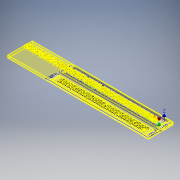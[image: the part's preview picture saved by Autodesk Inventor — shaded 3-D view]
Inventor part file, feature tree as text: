
AUTODESK INVENTOR PART (.ipt)
format: ipt  version: 2018.3 (Build 223284000, 284)  size: 20,308,992 bytes
history: native  units: in
note: dims shown in document units (in); Inventor stores cm internally (conversion verified against a paired STEP export)
features: other x459, extrude x4, plane x2, pattern_linear x2, hole x1
ambient origin geometry x8: Origin, YZ Plane, XZ Plane, XY Plane, X Axis, Y Axis, Z Axis, Center Point
bodies: Solid1 (feature_tree), Solid10 (feature_tree), Solid11 (feature_tree), Solid12 (feature_tree), Solid13 (feature_tree), Solid22 (feature_tree), Solid23 (feature_tree), Solid24 (feature_tree), Solid29 (feature_tree), Solid30 (feature_tree), Solid31 (feature_tree), Solid32 (feature_tree), Solid33 (feature_tree), Solid34 (feature_tree), Solid35 (feature_tree), Solid36 (feature_tree), Solid37 (feature_tree), Solid38 (feature_tree), Solid49 (feature_tree), Solid50 (feature_tree), Solid59 (feature_tree), Solid60 (feature_tree), Solid71 (feature_tree), Solid72 (feature_tree), Solid85 (feature_tree), Solid86 (feature_tree), Solid87 (feature_tree), Solid88 (feature_tree), Solid89 (feature_tree), Solid90 (feature_tree), Solid91 (feature_tree), Solid92 (feature_tree), Solid93 (feature_tree), Solid94 (feature_tree), Solid95 (feature_tree), Solid96 (feature_tree), Solid97 (feature_tree), Solid98 (feature_tree), Solid99 (feature_tree), Solid100 (feature_tree), Solid101 (feature_tree), Solid102 (feature_tree), Solid103 (feature_tree), Solid104 (feature_tree), Solid105 (feature_tree), Solid106 (feature_tree), Solid107 (feature_tree), Solid108 (feature_tree), Solid109 (feature_tree), Solid110 (feature_tree), Solid111 (feature_tree), Solid112 (feature_tree), Solid113 (feature_tree), Solid114 (feature_tree), Solid115 (feature_tree), Solid116 (feature_tree), Solid117 (feature_tree), Solid118 (feature_tree), Solid119 (feature_tree), Solid120 (feature_tree), Solid121 (feature_tree), Solid122 (feature_tree), Solid123 (feature_tree), Solid124 (feature_tree), Solid125 (feature_tree), Solid126 (feature_tree), Solid127 (feature_tree), Solid128 (feature_tree), Solid129 (feature_tree), Solid130 (feature_tree), Solid131 (feature_tree), Solid132 (feature_tree), Solid133 (feature_tree), Solid134 (feature_tree), Solid135 (feature_tree), Solid136 (feature_tree), Solid137 (feature_tree), Solid138 (feature_tree), Solid139 (feature_tree), Solid140 (feature_tree), Solid141 (feature_tree), Solid142 (feature_tree), Solid143 (feature_tree), Solid144 (feature_tree), Solid145 (feature_tree), Solid146 (feature_tree), Solid147 (feature_tree), Solid148 (feature_tree), Solid149 (feature_tree), Solid150 (feature_tree), Solid151 (feature_tree), Solid152 (feature_tree), Solid153 (feature_tree), Solid154 (feature_tree), Solid155 (feature_tree), Solid156 (feature_tree), Solid157 (feature_tree), Solid158 (feature_tree), Solid159 (feature_tree), Solid160 (feature_tree), Solid161 (feature_tree), Solid162 (feature_tree), Solid163 (feature_tree), Solid164 (feature_tree), Solid165 (feature_tree), Solid166 (feature_tree), Solid167 (feature_tree), Solid168 (feature_tree), Solid169 (feature_tree), Solid170 (feature_tree), Solid171 (feature_tree), Solid172 (feature_tree), Solid173 (feature_tree), Solid174 (feature_tree), Solid175 (feature_tree), Solid176 (feature_tree), Solid177 (feature_tree), Solid178 (feature_tree), Solid179 (feature_tree), Solid180 (feature_tree), Solid181 (feature_tree), Solid182 (feature_tree), Solid183 (feature_tree), Solid184 (feature_tree), Solid185 (feature_tree), Solid186 (feature_tree), Solid187 (feature_tree), Solid188 (feature_tree), Solid189 (feature_tree), Solid190 (feature_tree), Solid191 (feature_tree), Solid192 (feature_tree), Solid193 (feature_tree), Solid194 (feature_tree), Solid195 (feature_tree), Solid196 (feature_tree), Solid197 (feature_tree), Solid198 (feature_tree), Solid199 (feature_tree), Solid200 (feature_tree), Solid201 (feature_tree), Solid202 (feature_tree), Solid203 (feature_tree), Solid204 (feature_tree), Solid205 (feature_tree), Solid206 (feature_tree), Solid207 (feature_tree), Solid208 (feature_tree), Solid209 (feature_tree), Solid210 (feature_tree)
feature tree (468):
  other  "Button Fixture Assembly.iam"
  other  "Button Fixture Base.ipt:1"
  other  "Case Buttons CAM.ipt:9"
  other  "Case Buttons CAM.ipt:10"
  other  "Case Buttons CAM.ipt:11"
  other  "Case Buttons CAM.ipt:12"
  other  "Case Buttons CAM.ipt:17"
  other  "Case Buttons CAM.ipt:18"
  other  "Case Buttons CAM.ipt:19"
  other  "Case Buttons CAM.ipt:20"
  other  "Case Buttons CAM.ipt:25"
  other  "Case Buttons CAM.ipt:26"
  other  "Case Buttons CAM.ipt:27"
  other  "Case Buttons CAM.ipt:28"
  other  "Case Buttons CAM.ipt:29"
  other  "Case Buttons CAM.ipt:30"
  other  "Case Buttons CAM.ipt:31"
  other  "Case Buttons CAM.ipt:32"
  other  "Case Buttons CAM.ipt:41"
  other  "Case Buttons CAM.ipt:42"
  other  "Case Buttons CAM.ipt:53"
  other  "Case Buttons CAM.ipt:54"
  other  "Case Buttons CAM.ipt:64"
  other  "Case Buttons CAM.ipt:65"
  other  "Case Buttons CAM.ipt:76"
  other  "Case Buttons CAM.ipt:77"
  other  "Case Buttons CAM.ipt:90"
  other  "Case Buttons CAM.ipt:91"
  other  "Case Buttons CAM.ipt:92"
  other  "Case Buttons CAM.ipt:93"
  other  "Case Buttons CAM.ipt:94"
  other  "Case Buttons CAM.ipt:95"
  other  "Case Buttons CAM.ipt:108"
  other  "Case Buttons CAM.ipt:109"
  other  "Case Buttons CAM.ipt:110"
  other  "Case Buttons CAM.ipt:111"
  other  "Case Buttons CAM.ipt:112"
  other  "Case Buttons CAM.ipt:113"
  other  "Case Buttons CAM.ipt:126"
  other  "Case Buttons CAM.ipt:127"
  other  "Case Buttons CAM.ipt:128"
  other  "Case Buttons CAM.ipt:129"
  other  "Case Buttons CAM.ipt:130"
  other  "Case Buttons CAM.ipt:131"
  other  "Case Buttons CAM.ipt:132"
  other  "Case Buttons CAM.ipt:133"
  other  "Case Buttons CAM.ipt:134"
  other  "Case Buttons CAM.ipt:135"
  other  "Case Buttons CAM.ipt:136"
  other  "Case Buttons CAM.ipt:137"
  other  "Case Buttons CAM.ipt:138"
  other  "Case Buttons CAM.ipt:139"
  other  "Case Buttons CAM.ipt:140"
  other  "Case Buttons CAM.ipt:141"
  other  "Case Buttons CAM.ipt:142"
  other  "Case Buttons CAM.ipt:143"
  other  "Case Buttons CAM.ipt:144"
  other  "Case Buttons CAM.ipt:145"
  other  "Case Buttons CAM.ipt:146"
  other  "Case Buttons CAM.ipt:147"
  other  "Case Buttons CAM.ipt:148"
  other  "Case Buttons CAM.ipt:149"
  other  "Case Buttons CAM.ipt:150"
  other  "Case Buttons CAM.ipt:151"
  other  "Case Buttons CAM.ipt:152"
  other  "Case Buttons CAM.ipt:153"
  other  "Case Buttons CAM.ipt:154"
  other  "Case Buttons CAM.ipt:155"
  other  "Case Buttons CAM.ipt:156"
  other  "Case Buttons CAM.ipt:157"
  other  "Case Buttons CAM.ipt:158"
  other  "Case Buttons CAM.ipt:159"
  other  "Case Buttons CAM.ipt:160"
  other  "Case Buttons CAM.ipt:161"
  other  "Case Buttons CAM.ipt:162"
  other  "Case Buttons CAM.ipt:163"
  other  "Case Buttons CAM.ipt:164"
  other  "Case Buttons CAM.ipt:165"
  other  "Case Buttons CAM.ipt:166"
  other  "Case Buttons CAM.ipt:167"
  other  "Case Buttons CAM.ipt:168"
  other  "Case Buttons CAM.ipt:169"
  other  "Case Buttons CAM.ipt:170"
  other  "Case Buttons CAM.ipt:171"
  other  "Case Buttons CAM.ipt:172"
  other  "Case Buttons CAM.ipt:173"
  other  "Case Buttons CAM.ipt:174"
  other  "Case Buttons CAM.ipt:175"
  other  "Case Buttons CAM.ipt:176"
  other  "Case Buttons CAM.ipt:177"
  other  "Case Buttons CAM.ipt:178"
  other  "Case Buttons CAM.ipt:179"
  other  "Case Buttons CAM.ipt:180"
  other  "Case Buttons CAM.ipt:181"
  other  "Case Buttons CAM.ipt:182"
  other  "Case Buttons CAM.ipt:183"
  other  "Case Buttons CAM.ipt:184"
  other  "Case Buttons CAM.ipt:185"
  other  "Case Buttons CAM.ipt:186"
  other  "Case Buttons CAM.ipt:187"
  other  "Case Buttons CAM.ipt:188"
  other  "Case Buttons CAM.ipt:189"
  other  "Case Buttons CAM.ipt:190"
  other  "Case Buttons CAM.ipt:191"
  other  "Case Buttons CAM.ipt:192"
  other  "Case Buttons CAM.ipt:193"
  other  "Case Buttons CAM.ipt:194"
  other  "Case Buttons CAM.ipt:195"
  other  "Case Buttons CAM.ipt:196"
  other  "Case Buttons CAM.ipt:197"
  other  "Case Buttons CAM.ipt:198"
  other  "Case Buttons CAM.ipt:199"
  other  "Case Buttons CAM.ipt:200"
  other  "Case Buttons CAM.ipt:201"
  other  "Case Buttons CAM.ipt:202"
  other  "Case Buttons CAM.ipt:203"
  other  "Case Buttons CAM.ipt:204"
  other  "Case Buttons CAM.ipt:205"
  other  "Case Buttons CAM.ipt:206"
  other  "Case Buttons CAM.ipt:207"
  other  "Case Buttons CAM.ipt:208"
  other  "Case Buttons CAM.ipt:209"
  other  "Case Buttons CAM.ipt:210"
  other  "Case Buttons CAM.ipt:211"
  other  "Case Buttons CAM.ipt:212"
  other  "Case Buttons CAM.ipt:213"
  other  "Case Buttons CAM.ipt:214"
  other  "Case Buttons CAM.ipt:215"
  other  "Case Buttons CAM.ipt:216"
  other  "Case Buttons CAM.ipt:217"
  other  "Case Buttons CAM.ipt:218"
  other  "Case Buttons CAM.ipt:219"
  other  "Case Buttons CAM.ipt:220"
  other  "Case Buttons CAM.ipt:221"
  other  "Case Buttons CAM.ipt:222"
  other  "Case Buttons CAM.ipt:223"
  other  "Case Buttons CAM.ipt:224"
  other  "Case Buttons CAM.ipt:225"
  other  "Case Buttons CAM.ipt:226"
  other  "Case Buttons CAM.ipt:227"
  other  "Case Buttons CAM.ipt:228"
  other  "Case Buttons CAM.ipt:229"
  other  "Case Buttons CAM.ipt:230"
  other  "Case Buttons CAM.ipt:231"
  other  "Case Buttons CAM.ipt:232"
  other  "Case Buttons CAM.ipt:233"
  other  "Case Buttons CAM.ipt:234"
  other  "Case Buttons CAM.ipt:235"
  other  "Case Buttons CAM.ipt:236"
  other  "Case Buttons CAM.ipt:237"
  other  "Case Buttons CAM.ipt:238"
  other  "Case Buttons CAM.ipt:239"
  plane  "Work Plane1"
  plane  "Work Plane3"
  extrude  "Extrusion20"  Depth=0.3937in
  extrude  "Extrusion19"  Depth=0.3in TaperAngle=0.0deg
  hole  "Hole1"  [1 undecoded]
  pattern_linear  "Rectangular Pattern6"  Spacing1=0.0in  [1 undecoded]
  pattern_linear  "Rectangular Pattern7"  Count1=3 Spacing1=7.75in
  other  "Hold Down Sketch 1"
  other  "Hold Down Sketch 2"
  extrude  "Extrusion22"  Depth=0.0156in TaperAngle=0.0deg
  extrude  "Extrusion23"  Depth=0.0156in TaperAngle=0.0deg
  other  "Origin Sketch"
  other  "Vacuum Sketch"
  other  "Vacuum Sketch_1"
  other  "Vacuum Sketch_2"
  other  "Vacuum Sketch_3"
  other  "Button Peg Sketch"
  other  "Button Peg Sketch_1"
  other  "Button Peg Sketch_2"
  other  "Button Peg Sketch_3"
  other  "First Contour Solid"
  other  "Vacuum Sketch_4"
  other  "Button Peg Sketch_8"
  other  "Vacuum Sketch_5"
  other  "Button Peg Sketch_9"
  other  "Vacuum Sketch_6"
  other  "Button Peg Sketch_10"
  other  "Vacuum Sketch_7"
  other  "Button Peg Sketch_11"
  other  "Vacuum Sketch_8"
  other  "Button Peg Sketch_12"
  other  "Vacuum Sketch_9"
  other  "Button Peg Sketch_13"
  other  "Vacuum Sketch_10"
  other  "Button Peg Sketch_14"
  other  "Vacuum Sketch_11"
  other  "Button Peg Sketch_15"
  other  "Vacuum Sketch_12"
  other  "Button Peg Sketch_16"
  other  "Vacuum Sketch_13"
  other  "Button Peg Sketch_17"
  other  "Vacuum Sketch_14"
  other  "Button Peg Sketch_18"
  other  "Vacuum Sketch_15"
  other  "Button Peg Sketch_19"
  other  "Contour Boundary Sketch"
  other  "Pocket Boundary Sketch"
  other  "Contour Standoff Boundary Sketch"
  other  "Vacuum Sketch_16"
  other  "Button Peg Sketch_20"
  other  "Vacuum Sketch_17"
  other  "Button Peg Sketch_21"
  other  "Vacuum Sketch_28"
  other  "Button Peg Sketch_32"
  other  "Vacuum Sketch_29"
  other  "Button Peg Sketch_33"
  other  "Vacuum Sketch_38"
  other  "Button Peg Sketch_42"
  other  "Vacuum Sketch_39"
  other  "Button Peg Sketch_43"
  other  "Vacuum Sketch_50"
  other  "Button Peg Sketch_54"
  other  "Vacuum Sketch_51"
  other  "Button Peg Sketch_55"
  other  "Vacuum Sketch_52"
  other  "Button Peg Sketch_66"
  other  "Vacuum Sketch_53"
  other  "Button Peg Sketch_67"
  other  "Vacuum Sketch_54"
  other  "Button Peg Sketch_68"
  other  "Vacuum Sketch_55"
  other  "Button Peg Sketch_69"
  other  "Vacuum Sketch_56"
  other  "Button Peg Sketch_70"
  other  "Vacuum Sketch_57"
  other  "Button Peg Sketch_71"
  other  "Vacuum Sketch_58"
  other  "Button Peg Sketch_72"
  other  "Vacuum Sketch_59"
  other  "Button Peg Sketch_73"
  other  "Vacuum Sketch_60"
  other  "Button Peg Sketch_74"
  other  "Vacuum Sketch_61"
  other  "Button Peg Sketch_75"
  other  "Vacuum Sketch_62"
  other  "Button Peg Sketch_76"
  other  "Vacuum Sketch_63"
  other  "Button Peg Sketch_77"
  other  "Vacuum Sketch_64"
  other  "Button Peg Sketch_78"
  other  "Vacuum Sketch_65"
  other  "Button Peg Sketch_79"
  other  "Vacuum Sketch_66"
  other  "Button Peg Sketch_80"
  other  "Vacuum Sketch_67"
  other  "Button Peg Sketch_81"
  other  "Vacuum Sketch_68"
  other  "Button Peg Sketch_82"
  other  "Vacuum Sketch_69"
  other  "Button Peg Sketch_83"
  other  "Vacuum Sketch_70"
  other  "Button Peg Sketch_84"
  other  "Vacuum Sketch_71"
  other  "Button Peg Sketch_85"
  other  "Vacuum Sketch_72"
  other  "Button Peg Sketch_86"
  other  "Vacuum Sketch_73"
  other  "Button Peg Sketch_87"
  other  "Vacuum Sketch_74"
  other  "Button Peg Sketch_88"
  other  "Vacuum Sketch_75"
  other  "Button Peg Sketch_89"
  other  "Vacuum Sketch_76"
  other  "Button Peg Sketch_90"
  other  "Vacuum Sketch_77"
  other  "Button Peg Sketch_91"
  other  "Vacuum Sketch_78"
  other  "Button Peg Sketch_92"
  other  "Vacuum Sketch_79"
  other  "Button Peg Sketch_93"
  other  "Vacuum Sketch_80"
  other  "Button Peg Sketch_94"
  other  "Vacuum Sketch_81"
  other  "Button Peg Sketch_95"
  other  "Vacuum Sketch_82"
  other  "Button Peg Sketch_96"
  other  "Vacuum Sketch_83"
  other  "Button Peg Sketch_97"
  other  "Vacuum Sketch_84"
  other  "Button Peg Sketch_98"
  other  "Vacuum Sketch_85"
  other  "Button Peg Sketch_99"
  other  "Vacuum Sketch_86"
  other  "Button Peg Sketch_100"
  other  "Vacuum Sketch_87"
  other  "Button Peg Sketch_101"
  other  "Vacuum Sketch_88"
  other  "Button Peg Sketch_102"
  other  "Vacuum Sketch_89"
  other  "Button Peg Sketch_103"
  other  "Vacuum Sketch_90"
  other  "Button Peg Sketch_104"
  other  "Vacuum Sketch_91"
  other  "Button Peg Sketch_105"
  other  "Vacuum Sketch_92"
  other  "Button Peg Sketch_106"
  other  "Vacuum Sketch_93"
  other  "Button Peg Sketch_107"
  other  "Vacuum Sketch_94"
  other  "Button Peg Sketch_108"
  other  "Vacuum Sketch_95"
  other  "Button Peg Sketch_109"
  other  "Vacuum Sketch_96"
  other  "Button Peg Sketch_110"
  other  "Vacuum Sketch_97"
  other  "Button Peg Sketch_111"
  other  "Vacuum Sketch_98"
  other  "Button Peg Sketch_112"
  other  "Vacuum Sketch_99"
  other  "Button Peg Sketch_113"
  other  "Vacuum Sketch_100"
  other  "Button Peg Sketch_114"
  other  "Vacuum Sketch_101"
  other  "Button Peg Sketch_115"
  other  "Vacuum Sketch_102"
  other  "Button Peg Sketch_116"
  other  "Vacuum Sketch_103"
  other  "Button Peg Sketch_117"
  other  "Vacuum Sketch_104"
  other  "Button Peg Sketch_118"
  other  "Vacuum Sketch_105"
  other  "Button Peg Sketch_119"
  other  "Vacuum Sketch_106"
  other  "Button Peg Sketch_120"
  other  "Vacuum Sketch_107"
  other  "Button Peg Sketch_121"
  other  "Vacuum Sketch_108"
  other  "Button Peg Sketch_122"
  other  "Vacuum Sketch_109"
  other  "Button Peg Sketch_123"
  other  "Vacuum Sketch_110"
  other  "Button Peg Sketch_124"
  other  "Vacuum Sketch_111"
  other  "Button Peg Sketch_125"
  other  "Vacuum Sketch_112"
  other  "Button Peg Sketch_126"
  other  "Vacuum Sketch_113"
  other  "Button Peg Sketch_127"
  other  "Vacuum Sketch_114"
  other  "Button Peg Sketch_128"
  other  "Vacuum Sketch_115"
  other  "Button Peg Sketch_129"
  other  "Vacuum Sketch_116"
  other  "Button Peg Sketch_130"
  other  "Vacuum Sketch_117"
  other  "Button Peg Sketch_131"
  other  "Vacuum Sketch_118"
  other  "Button Peg Sketch_132"
  other  "Vacuum Sketch_119"
  other  "Button Peg Sketch_133"
  other  "Vacuum Sketch_120"
  other  "Button Peg Sketch_134"
  other  "Vacuum Sketch_121"
  other  "Button Peg Sketch_135"
  other  "Vacuum Sketch_122"
  other  "Button Peg Sketch_136"
  other  "Vacuum Sketch_123"
  other  "Button Peg Sketch_137"
  other  "Vacuum Sketch_124"
  other  "Button Peg Sketch_138"
  other  "Vacuum Sketch_125"
  other  "Button Peg Sketch_139"
  other  "Vacuum Sketch_126"
  other  "Button Peg Sketch_140"
  other  "Vacuum Sketch_127"
  other  "Button Peg Sketch_141"
  other  "Vacuum Sketch_128"
  other  "Button Peg Sketch_142"
  other  "Vacuum Sketch_129"
  other  "Button Peg Sketch_143"
  other  "Vacuum Sketch_130"
  other  "Button Peg Sketch_144"
  other  "Vacuum Sketch_131"
  other  "Button Peg Sketch_145"
  other  "Vacuum Sketch_132"
  other  "Button Peg Sketch_146"
  other  "Vacuum Sketch_133"
  other  "Button Peg Sketch_147"
  other  "Vacuum Sketch_134"
  other  "Button Peg Sketch_148"
  other  "Vacuum Sketch_135"
  other  "Button Peg Sketch_149"
  other  "Vacuum Sketch_136"
  other  "Button Peg Sketch_150"
  other  "Vacuum Sketch_137"
  other  "Button Peg Sketch_151"
  other  "Vacuum Sketch_138"
  other  "Button Peg Sketch_152"
  other  "Vacuum Sketch_139"
  other  "Button Peg Sketch_153"
  other  "Vacuum Sketch_140"
  other  "Button Peg Sketch_154"
  other  "Vacuum Sketch_141"
  other  "Button Peg Sketch_155"
  other  "Vacuum Sketch_142"
  other  "Button Peg Sketch_156"
  other  "Vacuum Sketch_143"
  other  "Button Peg Sketch_157"
  other  "Vacuum Sketch_144"
  other  "Button Peg Sketch_158"
  other  "Vacuum Sketch_145"
  other  "Button Peg Sketch_159"
  other  "Vacuum Sketch_146"
  other  "Button Peg Sketch_160"
  other  "Vacuum Sketch_147"
  other  "Button Peg Sketch_161"
  other  "Vacuum Sketch_148"
  other  "Button Peg Sketch_162"
  other  "Vacuum Sketch_149"
  other  "Button Peg Sketch_163"
  other  "Vacuum Sketch_150"
  other  "Button Peg Sketch_164"
  other  "Vacuum Sketch_151"
  other  "Button Peg Sketch_165"
  other  "Vacuum Sketch_152"
  other  "Button Peg Sketch_166"
  other  "Vacuum Sketch_153"
  other  "Button Peg Sketch_167"
  other  "Vacuum Sketch_154"
  other  "Button Peg Sketch_168"
  other  "Vacuum Sketch_155"
  other  "Button Peg Sketch_169"
  other  "Vacuum Sketch_156"
  other  "Button Peg Sketch_170"
  other  "Vacuum Sketch_157"
  other  "Button Peg Sketch_171"
  other  "Vacuum Sketch_158"
  other  "Button Peg Sketch_172"
  other  "Vacuum Sketch_159"
  other  "Button Peg Sketch_173"
  other  "Vacuum Sketch_160"
  other  "Button Peg Sketch_174"
  other  "Vacuum Sketch_161"
  other  "Button Peg Sketch_175"
  other  "Vacuum Sketch_162"
  other  "Button Peg Sketch_176"
  other  "Vacuum Sketch_163"
  other  "Button Peg Sketch_177"
  other  "Vacuum Sketch_164"
  other  "Button Peg Sketch_178"
  other  "Vacuum Sketch_165"
  other  "Button Peg Sketch_179"
  other  "Vacuum Sketch_166"
  other  "Button Peg Sketch_180"
  other  "Vacuum Sketch_167"
  other  "Button Peg Sketch_181"
  other  "Vacuum Sketch_168"
  other  "Button Peg Sketch_182"
  other  "Vacuum Sketch_169"
  other  "Button Peg Sketch_183"
  other  "Vacuum Sketch_170"
  other  "Button Peg Sketch_184"
  other  "Vacuum Sketch_171"
  other  "Button Peg Sketch_185"
  other  "Vacuum Sketch_172"
  other  "Button Peg Sketch_186"
  other  "Vacuum Sketch_173"
  other  "Button Peg Sketch_187"
  other  "Vacuum Sketch_174"
  other  "Button Peg Sketch_188"
  other  "Vacuum Sketch_175"
  other  "Button Peg Sketch_189"
  other  "Vacuum Sketch_176"
  other  "Button Peg Sketch_190"
  other  "Vacuum Sketch_177"
  other  "Button Peg Sketch_191"
note: 2 required parameter values undecoded (feature->parameter linkage not recoverable at this tier; creation-order binding heuristic only, values carry confidence <= 0.55)
